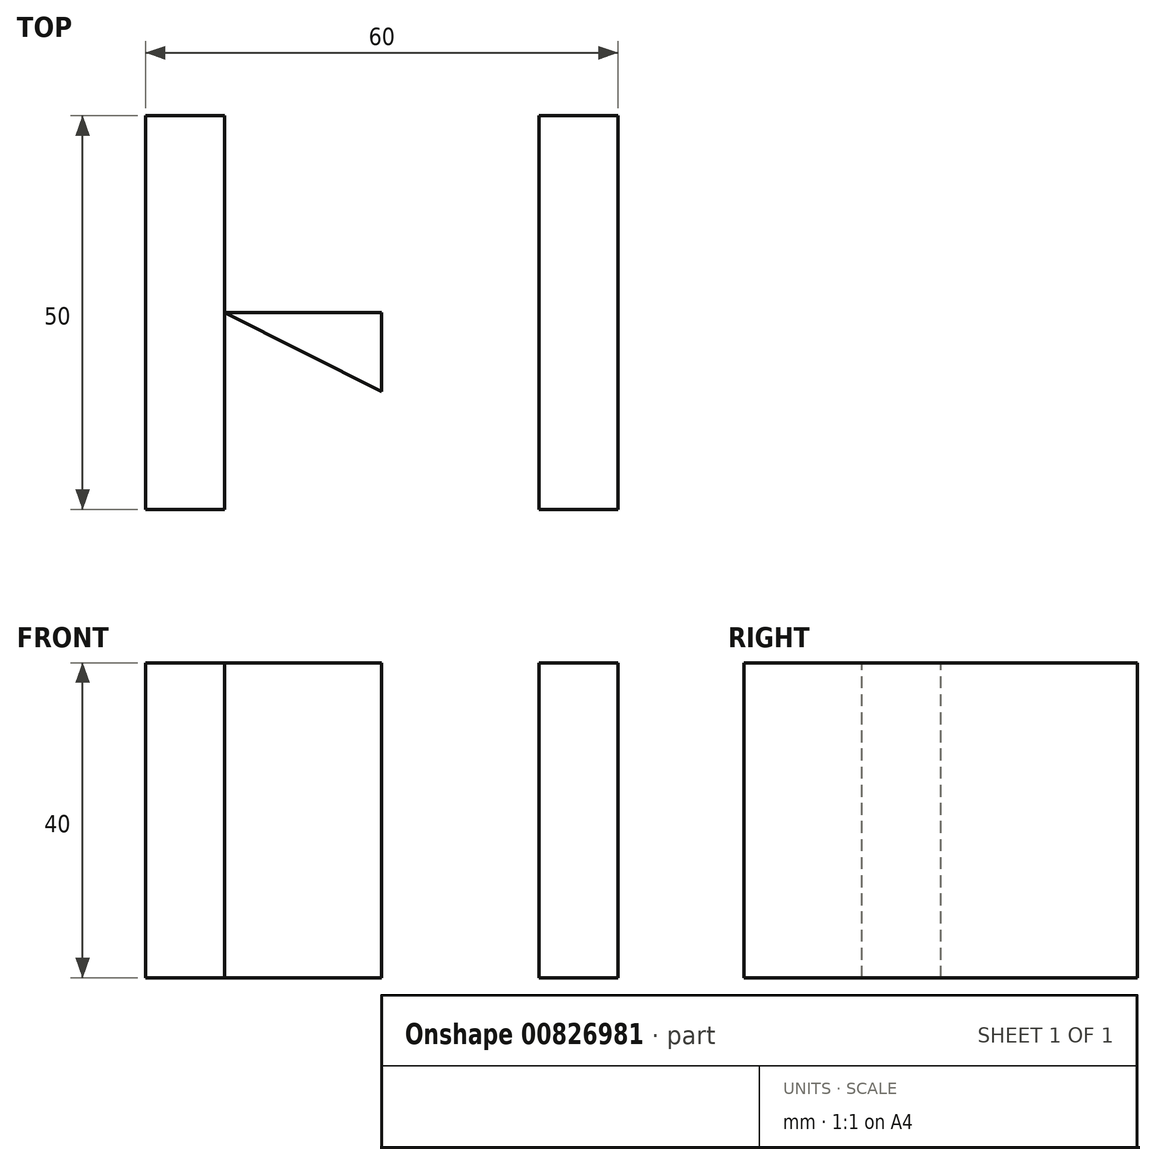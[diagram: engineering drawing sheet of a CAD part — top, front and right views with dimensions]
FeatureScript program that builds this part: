
annotation { "Feature Type Name" : "Feature", "Feature Type Description" : "" }
export const myFeature = defineFeature(function(context is Context, id is Id, definition is map)
    precondition{}
    {
        {
            var Q0;
            Q0=qCreatedBy(makeId("Top.planeOp"),FACE);
            var sketch = newSketch(context, id + "F0", { "sketchPlane" : qUnion([Q0])});
            skLineSegment(sketch, "E0", {"start": v(0, 0) * mm, "end": v(0, 50) * mm});
            skLineSegment(sketch, "E1", {"start": v(0, 50) * mm, "end": v(60, 50) * mm});
            skLineSegment(sketch, "E2", {"start": v(60, 50) * mm, "end": v(60, 0) * mm});
            skLineSegment(sketch, "E3", {"start": v(60, 0) * mm, "end": v(0, 0) * mm});
            skLineSegment(sketch, "E4", {"start": v(10, 50) * mm, "end": v(10, 0) * mm});
            skLineSegment(sketch, "E5", {"start": v(0, 25) * mm, "end": v(60, 25) * mm});
            skLineSegment(sketch, "E6", {"start": v(50, 50) * mm, "end": v(50, 0) * mm});
            skLineSegment(sketch, "E7", {"start": v(0, 15) * mm, "end": v(60, 15) * mm});
            skLineSegment(sketch, "E8", {"start": v(50, 50) * mm, "end": v(30, 50) * mm});
            skLineSegment(sketch, "E9", {"start": v(30, 50) * mm, "end": v(30, 0) * mm});
            skLineSegment(sketch, "E10", {"start": v(10, 50) * mm, "end": v(10, 25) * mm});
            skLineSegment(sketch, "E11", {"start": v(10, 25) * mm, "end": v(30, 15) * mm});
            skLineSegment(sketch, "E12", {"start": v(30, 15) * mm, "end": v(50, 25) * mm});
            skLineSegment(sketch, "E13", {"start": v(50, 25) * mm, "end": v(50, 50) * mm});
            skSolve(sketch);
        }
        {
            var Q0;
            {var subQ0=sQuery(id+"F0.wireOp",EDGE,"E3");var subQ1=sQuery(id+"F0.wireOp",EDGE,"E0");var subQ2=makeQuery(id+"F0.imprint","INTERSECT",VERTEX,{"derivedFrom":[subQ1,subQ0]});Q0=makeQuery(id+"F0.imprint","IMPRINT",FACE,{"disambiguationData":[TD([[makeQuery(id+"F0.imprint","IMPRINT",EDGE,{"disambiguationData":[TD([[subQ2,-1.0]])],"derivedFrom":subQ1}),-1.0]])]});}
            var Q1;
            {var subQ0=sQuery(id+"F0.wireOp",EDGE,"E5");var subQ1=sQuery(id+"F0.wireOp",EDGE,"E0");var subQ2=makeQuery(id+"F0.imprint","INTERSECT",VERTEX,{"derivedFrom":[subQ1,subQ0]});Q1=makeQuery(id+"F0.imprint","IMPRINT",FACE,{"disambiguationData":[TD([[makeQuery(id+"F0.imprint","IMPRINT",EDGE,{"disambiguationData":[TD([[subQ2,1.0]])],"derivedFrom":subQ1}),-1.0]])]});}
            var Q2;
            {var subQ0=sQuery(id+"F0.wireOp",EDGE,"E5");var subQ1=sQuery(id+"F0.wireOp",EDGE,"E0");var subQ2=makeQuery(id+"F0.imprint","INTERSECT",VERTEX,{"derivedFrom":[subQ1,subQ0]});Q2=makeQuery(id+"F0.imprint","IMPRINT",FACE,{"disambiguationData":[TD([[makeQuery(id+"F0.imprint","IMPRINT",EDGE,{"disambiguationData":[TD([[subQ2,-1.0]])],"derivedFrom":subQ1}),-1.0]])]});}
            var Q3;
            {var subQ0=sQuery(id+"F0.wireOp",EDGE,"E2");var subQ1=sQuery(id+"F0.wireOp",EDGE,"E1");var subQ2=makeQuery(id+"F0.imprint","INTERSECT",VERTEX,{"derivedFrom":[subQ1,subQ0]});Q3=makeQuery(id+"F0.imprint","IMPRINT",FACE,{"disambiguationData":[TD([[makeQuery(id+"F0.imprint","IMPRINT",EDGE,{"disambiguationData":[TD([[subQ2,1.0]])],"derivedFrom":subQ1}),-1.0]])]});}
            var Q4;
            {var subQ0=sQuery(id+"F0.wireOp",EDGE,"E7");var subQ1=sQuery(id+"F0.wireOp",EDGE,"E2");var subQ2=makeQuery(id+"F0.imprint","INTERSECT",VERTEX,{"derivedFrom":[subQ1,subQ0]});Q4=makeQuery(id+"F0.imprint","IMPRINT",FACE,{"disambiguationData":[TD([[makeQuery(id+"F0.imprint","IMPRINT",EDGE,{"disambiguationData":[TD([[subQ2,1.0]])],"derivedFrom":subQ1}),-1.0]])]});}
            var Q5;
            {var subQ0=sQuery(id+"F0.wireOp",EDGE,"E7");var subQ1=sQuery(id+"F0.wireOp",EDGE,"E2");var subQ2=makeQuery(id+"F0.imprint","INTERSECT",VERTEX,{"derivedFrom":[subQ1,subQ0]});Q5=makeQuery(id+"F0.imprint","IMPRINT",FACE,{"disambiguationData":[TD([[makeQuery(id+"F0.imprint","IMPRINT",EDGE,{"disambiguationData":[TD([[subQ2,-1.0]])],"derivedFrom":subQ1}),-1.0]])]});}
            var Q6;
            {var subQ3=sQuery(id+"F0.wireOp",EDGE,"E11");Q6=makeQuery(id+"F0.imprint","IMPRINT",FACE,{"disambiguationData":[TD([[makeQuery(id+"F0.imprint","IMPRINT",EDGE,{"derivedFrom":subQ3}),1.0]])]});}
            extrude(context, id + "F1", {"entities" : qUnion([Q0, Q1, Q2, Q3, Q4, Q5, Q6]), "depth" : -40 * mm, "offsetDistance" : 25 * mm});
        }
    });
